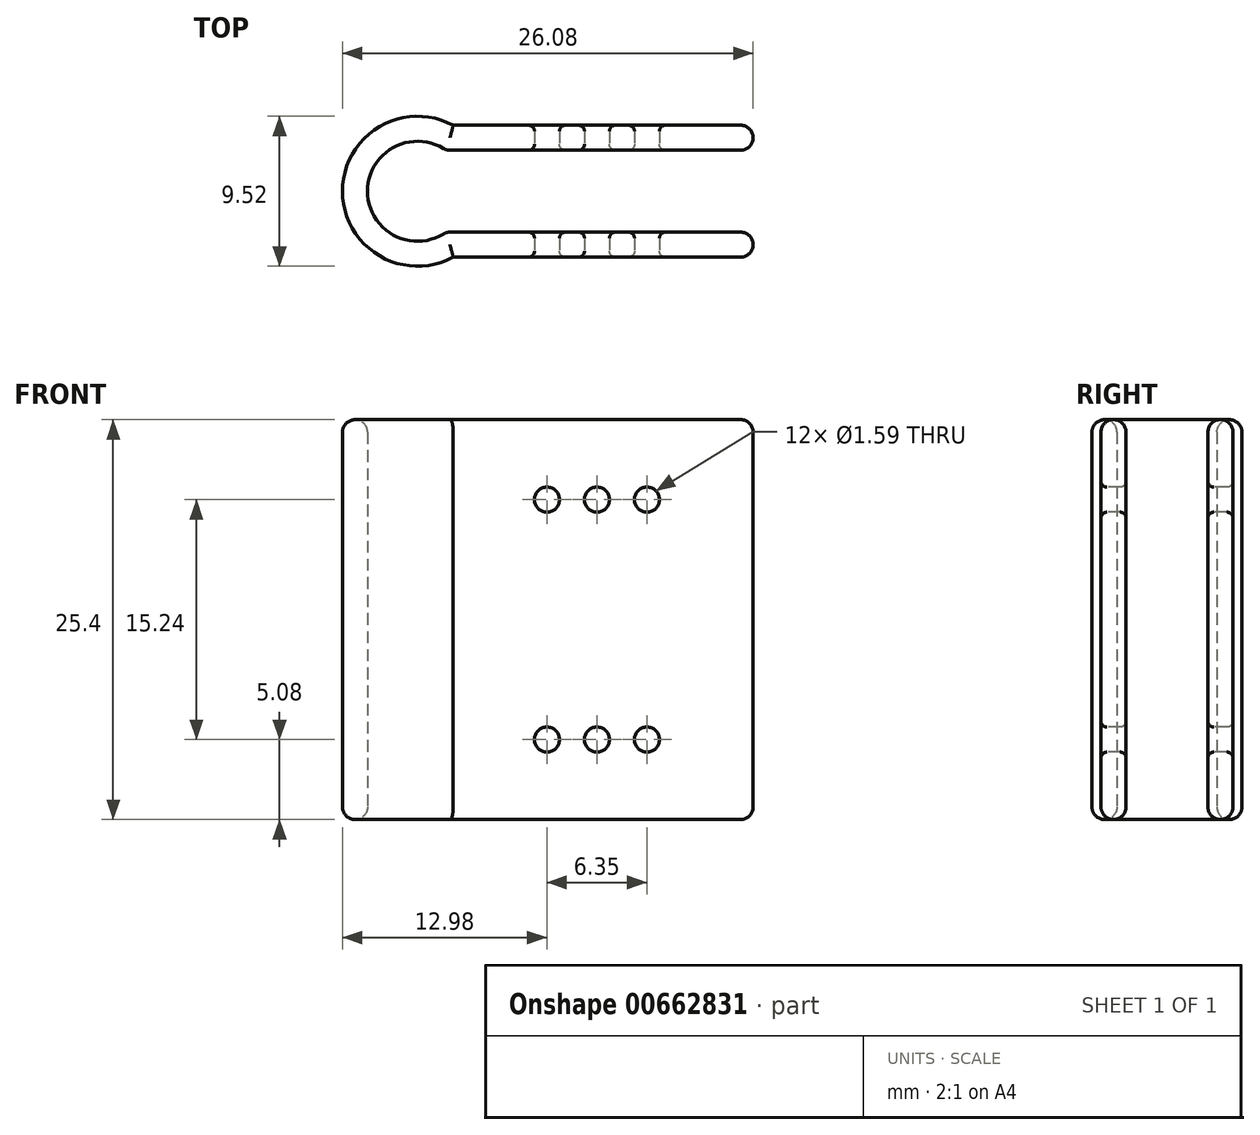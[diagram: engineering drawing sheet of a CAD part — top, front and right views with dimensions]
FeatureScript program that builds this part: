
annotation { "Feature Type Name" : "Feature", "Feature Type Description" : "" }
export const myFeature = defineFeature(function(context is Context, id is Id, definition is map)
    precondition{}
    {
        {
            var Q0;
            Q0=qCreatedBy(makeId("Top.planeOp"),FACE);
            var sketch = newSketch(context, id + "F0", { "sketchPlane" : qUnion([Q0])});
            skCircle(sketch, "E0", {"center": v(0, 0) * mm, "radius": 3.18 * mm});
            skCircle(sketch, "E1", {"center": v(0, 0) * mm, "radius": 4.76 * mm});
            skLineSegment(sketch, "E2", {"start": v(0, 0) * mm, "end": v(2.73, 3.9) * mm});
            skLineSegment(sketch, "E3", {"start": v(-3.18, 0) * mm, "end": v(3.18, 0) * mm, "construction": true});
            skLineSegment(sketch, "E4", {"start": v(0, 0) * mm, "end": v(2.73, -3.9) * mm});
            skLineSegment(sketch, "E5", {"start": v(2.27, 4.19) * mm, "end": v(21.32, 4.19) * mm});
            skLineSegment(sketch, "E6", {"start": v(21.32, 4.19) * mm, "end": v(21.32, 2.6) * mm});
            skLineSegment(sketch, "E7", {"start": v(21.32, 2.6) * mm, "end": v(1.82, 2.6) * mm});
            skLineSegment(sketch, "E8", {"start": v(1.82, -2.6) * mm, "end": v(21.32, -2.6) * mm});
            skLineSegment(sketch, "E9", {"start": v(21.32, -2.6) * mm, "end": v(21.32, -4.19) * mm});
            skLineSegment(sketch, "E10", {"start": v(21.32, -4.19) * mm, "end": v(2.27, -4.19) * mm});
            skSolve(sketch);
        }
        {
            var Q0;
            {var subQ0=sQuery(id+"F0.wireOp",EDGE,"E2");var subQ1=sQuery(id+"F0.wireOp",EDGE,"E0");var subQ2=makeQuery(id+"F0.imprint","INTERSECT",VERTEX,{"derivedFrom":[subQ1,subQ0]});Q0=makeQuery(id+"F0.imprint","IMPRINT",FACE,{"disambiguationData":[TD([[makeQuery(id+"F0.imprint","IMPRINT",EDGE,{"disambiguationData":[TD([[subQ2,-1.0]])],"derivedFrom":subQ1}),-1.0]])]});}
            var Q1;
            {var subQ0=sQuery(id+"F0.wireOp",EDGE,"E5");Q1=makeQuery(id+"F0.imprint","IMPRINT",FACE,{"disambiguationData":[TD([[makeQuery(id+"F0.imprint","IMPRINT",EDGE,{"derivedFrom":subQ0}),-1.0]])]});}
            var Q2;
            {var subQ0=sQuery(id+"F0.wireOp",EDGE,"E8");Q2=makeQuery(id+"F0.imprint","IMPRINT",FACE,{"disambiguationData":[TD([[makeQuery(id+"F0.imprint","IMPRINT",EDGE,{"derivedFrom":subQ0}),-1.0]])]});}
            var Q3;
            {var subQ0=sQuery(id+"F0.wireOp",EDGE,"E2");var subQ1=sQuery(id+"F0.wireOp",EDGE,"E1");var subQ2=makeQuery(id+"F0.imprint","INTERSECT",VERTEX,{"derivedFrom":[subQ1,subQ0]});Q3=makeQuery(id+"F0.imprint","IMPRINT",FACE,{"disambiguationData":[TD([[makeQuery(id+"F0.imprint","IMPRINT",EDGE,{"disambiguationData":[TD([[subQ2,1.0]])],"derivedFrom":subQ1}),1.0]])]});}
            var Q4;
            {var subQ0=sQuery(id+"F0.wireOp",EDGE,"E9");Q4=makeQuery(id+"F0.imprint","IMPRINT",FACE,{"disambiguationData":[TD([[makeQuery(id+"F0.imprint","IMPRINT",EDGE,{"derivedFrom":subQ0}),-1.0]])]});}
            extrude(context, id + "F1", {"entities" : qUnion([Q0, Q1, Q2, Q3, Q4]), "depth" : 25.4 * mm, "offsetDistance" : 25.4 * mm});
        }
        {
            var Q0;
            Q0=makeQuery(id+"F1.opExtrude","CAP_FACE",FACE,{"disambiguationData":[OSD([sQuery(id+"F0.wireOp",EDGE,"E0"),sQuery(id+"F0.wireOp",EDGE,"E1"),sQuery(id+"F0.wireOp",EDGE,"E2"),sQuery(id+"F0.wireOp",EDGE,"E4"),sQuery(id+"F0.wireOp",EDGE,"E5"),sQuery(id+"F0.wireOp",EDGE,"E6"),sQuery(id+"F0.wireOp",EDGE,"E7"),sQuery(id+"F0.wireOp",EDGE,"E8"),sQuery(id+"F0.wireOp",EDGE,"E9"),sQuery(id+"F0.wireOp",EDGE,"E10")])],"isStart":false});
            var Q1;
            Q1=makeQuery(id+"F1.opExtrude","CAP_FACE",FACE,{"disambiguationData":[OSD([sQuery(id+"F0.wireOp",EDGE,"E0"),sQuery(id+"F0.wireOp",EDGE,"E1"),sQuery(id+"F0.wireOp",EDGE,"E2"),sQuery(id+"F0.wireOp",EDGE,"E4"),sQuery(id+"F0.wireOp",EDGE,"E5"),sQuery(id+"F0.wireOp",EDGE,"E6"),sQuery(id+"F0.wireOp",EDGE,"E7"),sQuery(id+"F0.wireOp",EDGE,"E8"),sQuery(id+"F0.wireOp",EDGE,"E9"),sQuery(id+"F0.wireOp",EDGE,"E10")])],"isStart":true});
            var Q2;
            Q2=makeQuery(id+"F1.opExtrude","SWEPT_FACE",FACE,{"disambiguationData":[OSD([sQuery(id+"F0.wireOp",EDGE,"E6")])]});
            var Q3;
            Q3=makeQuery(id+"F1.opExtrude","SWEPT_FACE",FACE,{"disambiguationData":[OSD([sQuery(id+"F0.wireOp",EDGE,"E9")])]});
            var Q4;
            Q4=makeQuery(id+"F1.opExtrude","SWEPT_FACE",FACE,{"disambiguationData":[OSD([sQuery(id+"F0.wireOp",EDGE,"E2")])]});
            var Q5;
            Q5=makeQuery(id+"F1.opExtrude","SWEPT_FACE",FACE,{"disambiguationData":[OSD([sQuery(id+"F0.wireOp",EDGE,"E4")])]});
            var Q6;
            Q6=makeQuery(id+"F1.opExtrude","SWEPT_EDGE",EDGE,{"disambiguationData":[OSD([sQuery(id+"F0.wireOp",EDGE,"E0"),sQuery(id+"F0.wireOp",EDGE,"E4"),sQuery(id+"F0.wireOp",EDGE,"E8")])]});
            var Q7;
            Q7=makeQuery(id+"F1.opExtrude","SWEPT_EDGE",EDGE,{"disambiguationData":[OSD([sQuery(id+"F0.wireOp",EDGE,"E0"),sQuery(id+"F0.wireOp",EDGE,"E2"),sQuery(id+"F0.wireOp",EDGE,"E7")])]});
            fillet(context, id + "F2", {"entities" : qUnion([Q0, Q1, Q2, Q3, Q4, Q5, Q6, Q7]), "radius" : 0.8 * mm, "tangentPropagation" : true, "allowEdgeOverflow" : false});
        }
        {
            var Q0;
            Q0=makeQuery(id+"F1.opExtrude","SWEPT_FACE",FACE,{"disambiguationData":[OSD([sQuery(id+"F0.wireOp",EDGE,"E10")])]});
            var sketch = newSketch(context, id + "F3", { "sketchPlane" : qUnion([Q0])});
            skCircle(sketch, "E11", {"center": v(11.4, 12.7) * mm, "radius": 0.8 * mm});
            skPoint(sketch, "E11.centerSnap0", {"position": v(11.4, 24.6) * mm});
            skPoint(sketch, "E11.centerSnap1", {"position": v(20.52, 12.7) * mm});
            skCircle(sketch, "E12.0.1.0", {"center": v(11.4, 8.9) * mm, "radius": 0.8 * mm});
            skCircle(sketch, "E12.1.0.0", {"center": v(11.4, 16.51) * mm, "radius": 0.8 * mm});
            skCircle(sketch, "E12.2.0.0", {"center": v(11.4, 20.32) * mm, "radius": 0.8 * mm});
            skCircle(sketch, "E12.2.1.0", {"center": v(11.4, 16.51) * mm, "radius": 0.8 * mm});
            skLineSegment(sketch, "E12.direction1", {"start": v(11.4, 12.7) * mm, "end": v(11.4, 16.51) * mm, "construction": true});
            skLineSegment(sketch, "E12.direction2", {"start": v(11.4, 12.7) * mm, "end": v(11.4, 8.9) * mm, "construction": true});
            skCircle(sketch, "E13.0.0.2", {"center": v(11.4, 5.08) * mm, "radius": 0.8 * mm});
            skLineSegment(sketch, "E14", {"start": v(2.27, 12.7) * mm, "end": v(20.52, 12.7) * mm, "construction": true});
            skCircle(sketch, "E15.0.1.0", {"center": v(8.22, 12.7) * mm, "radius": 0.8 * mm});
            skCircle(sketch, "E15.1.0.0", {"center": v(14.57, 12.7) * mm, "radius": 0.8 * mm});
            skLineSegment(sketch, "E15.direction1", {"start": v(11.4, 12.7) * mm, "end": v(14.57, 12.7) * mm, "construction": true});
            skLineSegment(sketch, "E15.direction2", {"start": v(11.4, 12.7) * mm, "end": v(8.22, 12.7) * mm, "construction": true});
            skCircle(sketch, "E16.0.1.0", {"center": v(8.22, 8.9) * mm, "radius": 0.8 * mm});
            skCircle(sketch, "E16.0.2.0", {"center": v(8.22, 5.08) * mm, "radius": 0.8 * mm});
            skCircle(sketch, "E16.1.0.0", {"center": v(8.22, 16.51) * mm, "radius": 0.8 * mm});
            skCircle(sketch, "E16.1.2.0", {"center": v(8.22, 8.9) * mm, "radius": 0.8 * mm});
            skCircle(sketch, "E16.2.0.0", {"center": v(8.22, 20.32) * mm, "radius": 0.8 * mm});
            skCircle(sketch, "E16.2.1.0", {"center": v(8.22, 16.51) * mm, "radius": 0.8 * mm});
            skLineSegment(sketch, "E16.direction1", {"start": v(8.22, 12.7) * mm, "end": v(8.22, 16.51) * mm, "construction": true});
            skLineSegment(sketch, "E16.direction2", {"start": v(8.22, 12.7) * mm, "end": v(8.22, 8.9) * mm, "construction": true});
            skCircle(sketch, "E17.0.1.0", {"center": v(14.57, 16.51) * mm, "radius": 0.8 * mm});
            skCircle(sketch, "E17.0.2.0", {"center": v(14.57, 20.32) * mm, "radius": 0.8 * mm});
            skCircle(sketch, "E17.1.0.0", {"center": v(14.57, 8.9) * mm, "radius": 0.8 * mm});
            skCircle(sketch, "E17.1.2.0", {"center": v(14.57, 16.51) * mm, "radius": 0.8 * mm});
            skCircle(sketch, "E17.2.0.0", {"center": v(14.57, 5.08) * mm, "radius": 0.8 * mm});
            skCircle(sketch, "E17.2.1.0", {"center": v(14.57, 8.9) * mm, "radius": 0.8 * mm});
            skLineSegment(sketch, "E17.direction1", {"start": v(14.57, 12.7) * mm, "end": v(14.57, 8.9) * mm, "construction": true});
            skLineSegment(sketch, "E17.direction2", {"start": v(14.57, 12.7) * mm, "end": v(14.57, 16.51) * mm, "construction": true});
            skSolve(sketch);
        }
        {
            var Q0;
            Q0=makeQuery(id+"F3.imprint","IMPRINT",FACE,{"disambiguationData":[TD([[makeQuery(id+"F3.imprint","IMPRINT",EDGE,{"derivedFrom":sQuery(id+"F3.wireOp",EDGE,"E11")}),1.0]])]});
            var Q1;
            Q1=makeQuery(id+"F3.imprint","IMPRINT",FACE,{"disambiguationData":[TD([[makeQuery(id+"F3.imprint","IMPRINT",EDGE,{"derivedFrom":sQuery(id+"F3.wireOp",EDGE,"E15.1.0.0")}),1.0]])]});
            var Q2;
            Q2=makeQuery(id+"F3.imprint","IMPRINT",FACE,{"disambiguationData":[TD([[makeQuery(id+"F3.imprint","IMPRINT",EDGE,{"derivedFrom":sQuery(id+"F3.wireOp",EDGE,"E16.1.2.0")}),1.0]])]});
            var Q3;
            Q3=makeQuery(id+"F3.imprint","IMPRINT",FACE,{"disambiguationData":[TD([[makeQuery(id+"F3.imprint","IMPRINT",EDGE,{"derivedFrom":sQuery(id+"F3.wireOp",EDGE,"E12.0.1.0")}),1.0]])]});
            var Q4;
            Q4=makeQuery(id+"F3.imprint","IMPRINT",FACE,{"disambiguationData":[TD([[makeQuery(id+"F3.imprint","IMPRINT",EDGE,{"derivedFrom":sQuery(id+"F3.wireOp",EDGE,"E17.2.1.0")}),1.0]])]});
            var Q5;
            Q5=makeQuery(id+"F3.imprint","IMPRINT",FACE,{"disambiguationData":[TD([[makeQuery(id+"F3.imprint","IMPRINT",EDGE,{"derivedFrom":sQuery(id+"F3.wireOp",EDGE,"E13.0.0.2")}),1.0]])]});
            var Q6;
            Q6=makeQuery(id+"F3.imprint","IMPRINT",FACE,{"disambiguationData":[TD([[makeQuery(id+"F3.imprint","IMPRINT",EDGE,{"derivedFrom":sQuery(id+"F3.wireOp",EDGE,"E17.2.0.0")}),1.0]])]});
            var Q7;
            Q7=makeQuery(id+"F3.imprint","IMPRINT",FACE,{"disambiguationData":[TD([[makeQuery(id+"F3.imprint","IMPRINT",EDGE,{"derivedFrom":sQuery(id+"F3.wireOp",EDGE,"E15.0.1.0")}),1.0]])]});
            var Q8;
            Q8=makeQuery(id+"F3.imprint","IMPRINT",FACE,{"disambiguationData":[TD([[makeQuery(id+"F3.imprint","IMPRINT",EDGE,{"derivedFrom":sQuery(id+"F3.wireOp",EDGE,"E12.2.1.0")}),1.0]])]});
            var Q9;
            Q9=makeQuery(id+"F3.imprint","IMPRINT",FACE,{"disambiguationData":[TD([[makeQuery(id+"F3.imprint","IMPRINT",EDGE,{"derivedFrom":sQuery(id+"F3.wireOp",EDGE,"E17.1.2.0")}),1.0]])]});
            var Q10;
            Q10=makeQuery(id+"F3.imprint","IMPRINT",FACE,{"disambiguationData":[TD([[makeQuery(id+"F3.imprint","IMPRINT",EDGE,{"derivedFrom":sQuery(id+"F3.wireOp",EDGE,"E16.2.0.0")}),1.0]])]});
            var Q11;
            Q11=makeQuery(id+"F3.imprint","IMPRINT",FACE,{"disambiguationData":[TD([[makeQuery(id+"F3.imprint","IMPRINT",EDGE,{"derivedFrom":sQuery(id+"F3.wireOp",EDGE,"E12.2.0.0")}),1.0]])]});
            var Q12;
            Q12=makeQuery(id+"F3.imprint","IMPRINT",FACE,{"disambiguationData":[TD([[makeQuery(id+"F3.imprint","IMPRINT",EDGE,{"derivedFrom":sQuery(id+"F3.wireOp",EDGE,"E17.0.2.0")}),1.0]])]});
            var Q13;
            Q13=makeQuery(id+"F3.imprint","IMPRINT",FACE,{"disambiguationData":[TD([[makeQuery(id+"F3.imprint","IMPRINT",EDGE,{"derivedFrom":sQuery(id+"F3.wireOp",EDGE,"E16.2.1.0")}),1.0]])]});
            var Q14;
            Q14=makeQuery(id+"F3.imprint","IMPRINT",FACE,{"disambiguationData":[TD([[makeQuery(id+"F3.imprint","IMPRINT",EDGE,{"derivedFrom":sQuery(id+"F3.wireOp",EDGE,"E16.0.2.0")}),1.0]])]});
            extrude(context, id + "F4", {"entities" : qUnion([Q0, Q1, Q2, Q3, Q4, Q5, Q6, Q7, Q8, Q9, Q10, Q11, Q12, Q13, Q14]), "operationType" : NewBodyOperationType.REMOVE, "endBound" : BoundingType.THROUGH_ALL, "oppositeDirection" : true, "depth" : 25.4 * mm, "offsetDistance" : 25.4 * mm});
        }
        {
            var Q0;
            Q0=makeQuery(id+"F4.boolean.opBoolean","COPY",FACE,{"derivedFrom":makeQuery(id+"F4.opExtrude","SWEPT_FACE",FACE,{"disambiguationData":[OSD([sQuery(id+"F3.wireOp",EDGE,"E16.0.2.0")])]})});
            var Q1;
            Q1=makeQuery(id+"F4.boolean.opBoolean","COPY",FACE,{"derivedFrom":makeQuery(id+"F4.opExtrude","SWEPT_FACE",FACE,{"disambiguationData":[OSD([sQuery(id+"F3.wireOp",EDGE,"E13.0.0.2")])]})});
            var Q2;
            Q2=makeQuery(id+"F4.boolean.opBoolean","COPY",FACE,{"derivedFrom":makeQuery(id+"F4.opExtrude","SWEPT_FACE",FACE,{"disambiguationData":[OSD([sQuery(id+"F3.wireOp",EDGE,"E17.2.0.0")])]})});
            var Q3;
            Q3=makeQuery(id+"F4.boolean.opBoolean","COPY",FACE,{"derivedFrom":makeQuery(id+"F4.opExtrude","SWEPT_FACE",FACE,{"disambiguationData":[OSD([sQuery(id+"F3.wireOp",EDGE,"E17.2.1.0")])]})});
            var Q4;
            Q4=makeQuery(id+"F4.boolean.opBoolean","COPY",FACE,{"derivedFrom":makeQuery(id+"F4.opExtrude","SWEPT_FACE",FACE,{"disambiguationData":[OSD([sQuery(id+"F3.wireOp",EDGE,"E12.0.1.0")])]})});
            var Q5;
            Q5=makeQuery(id+"F4.boolean.opBoolean","COPY",FACE,{"derivedFrom":makeQuery(id+"F4.opExtrude","SWEPT_FACE",FACE,{"disambiguationData":[OSD([sQuery(id+"F3.wireOp",EDGE,"E16.1.2.0")])]})});
            var Q6;
            Q6=makeQuery(id+"F4.boolean.opBoolean","COPY",FACE,{"derivedFrom":makeQuery(id+"F4.opExtrude","SWEPT_FACE",FACE,{"disambiguationData":[OSD([sQuery(id+"F3.wireOp",EDGE,"E15.0.1.0")])]})});
            var Q7;
            Q7=makeQuery(id+"F4.boolean.opBoolean","COPY",FACE,{"derivedFrom":makeQuery(id+"F4.opExtrude","SWEPT_FACE",FACE,{"disambiguationData":[OSD([sQuery(id+"F3.wireOp",EDGE,"E11")])]})});
            var Q8;
            Q8=makeQuery(id+"F4.boolean.opBoolean","COPY",FACE,{"derivedFrom":makeQuery(id+"F4.opExtrude","SWEPT_FACE",FACE,{"disambiguationData":[OSD([sQuery(id+"F3.wireOp",EDGE,"E15.1.0.0")])]})});
            var Q9;
            Q9=makeQuery(id+"F4.boolean.opBoolean","COPY",FACE,{"derivedFrom":makeQuery(id+"F4.opExtrude","SWEPT_FACE",FACE,{"disambiguationData":[OSD([sQuery(id+"F3.wireOp",EDGE,"E17.1.2.0")])]})});
            var Q10;
            Q10=makeQuery(id+"F4.boolean.opBoolean","COPY",FACE,{"derivedFrom":makeQuery(id+"F4.opExtrude","SWEPT_FACE",FACE,{"disambiguationData":[OSD([sQuery(id+"F3.wireOp",EDGE,"E12.2.1.0")])]})});
            var Q11;
            Q11=makeQuery(id+"F4.boolean.opBoolean","COPY",FACE,{"derivedFrom":makeQuery(id+"F4.opExtrude","SWEPT_FACE",FACE,{"disambiguationData":[OSD([sQuery(id+"F3.wireOp",EDGE,"E16.2.1.0")])]})});
            var Q12;
            Q12=makeQuery(id+"F4.boolean.opBoolean","COPY",FACE,{"derivedFrom":makeQuery(id+"F4.opExtrude","SWEPT_FACE",FACE,{"disambiguationData":[OSD([sQuery(id+"F3.wireOp",EDGE,"E17.0.2.0")])]})});
            var Q13;
            Q13=makeQuery(id+"F4.boolean.opBoolean","COPY",FACE,{"derivedFrom":makeQuery(id+"F4.opExtrude","SWEPT_FACE",FACE,{"disambiguationData":[OSD([sQuery(id+"F3.wireOp",EDGE,"E12.2.0.0")])]})});
            var Q14;
            Q14=makeQuery(id+"F4.boolean.opBoolean","COPY",FACE,{"derivedFrom":makeQuery(id+"F4.opExtrude","SWEPT_FACE",FACE,{"disambiguationData":[OSD([sQuery(id+"F3.wireOp",EDGE,"E16.2.0.0")])]})});
            fillet(context, id + "F5", {"entities" : qUnion([Q0, Q1, Q2, Q3, Q4, Q5, Q6, Q7, Q8, Q9, Q10, Q11, Q12, Q13, Q14]), "radius" : 0.38 * mm, "tangentPropagation" : true, "allowEdgeOverflow" : false});
        }
    });
